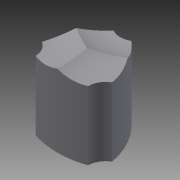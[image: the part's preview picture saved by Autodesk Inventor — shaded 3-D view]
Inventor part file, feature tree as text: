
AUTODESK INVENTOR PART (.ipt)
format: ipt  version: 2013 (Build 170138000, 138)  size: 120,320 bytes
history: native  units: mm
features: sketch x2, extrude x1, other x1, revolve x1, pattern_circular x1, projected_geometry x1
ambient origin geometry x8: Origin, YZ Plane, XZ Plane, XY Plane, X Axis, Y Axis, Z Axis, Center Point
bodies: Solid1 (feature_tree)
feature tree (7):
  extrude  "Extrusion1"  Depth=550.0mm
  other  "Work Axis1"
  revolve  "Revolution1"  [1 undecoded]
  pattern_circular  "Circular Pattern1"  Count=26  [1 undecoded]
  sketch  "Sketch1"  dims[d0=300.0mm d1=550.0mm]
  sketch  "Sketch2"  dims[d2=120.0mm d3=275.0mm d4=260.0mm d5=0.0mm d6=75.0mm d7=400.0mm d8=90.0deg d9=30.0mm d10=360.0deg]
  projected_geometry  "Project Cut Edges1"
note: 2 required parameter values undecoded (feature->parameter linkage not recoverable at this tier; creation-order binding heuristic only, values carry confidence <= 0.55)